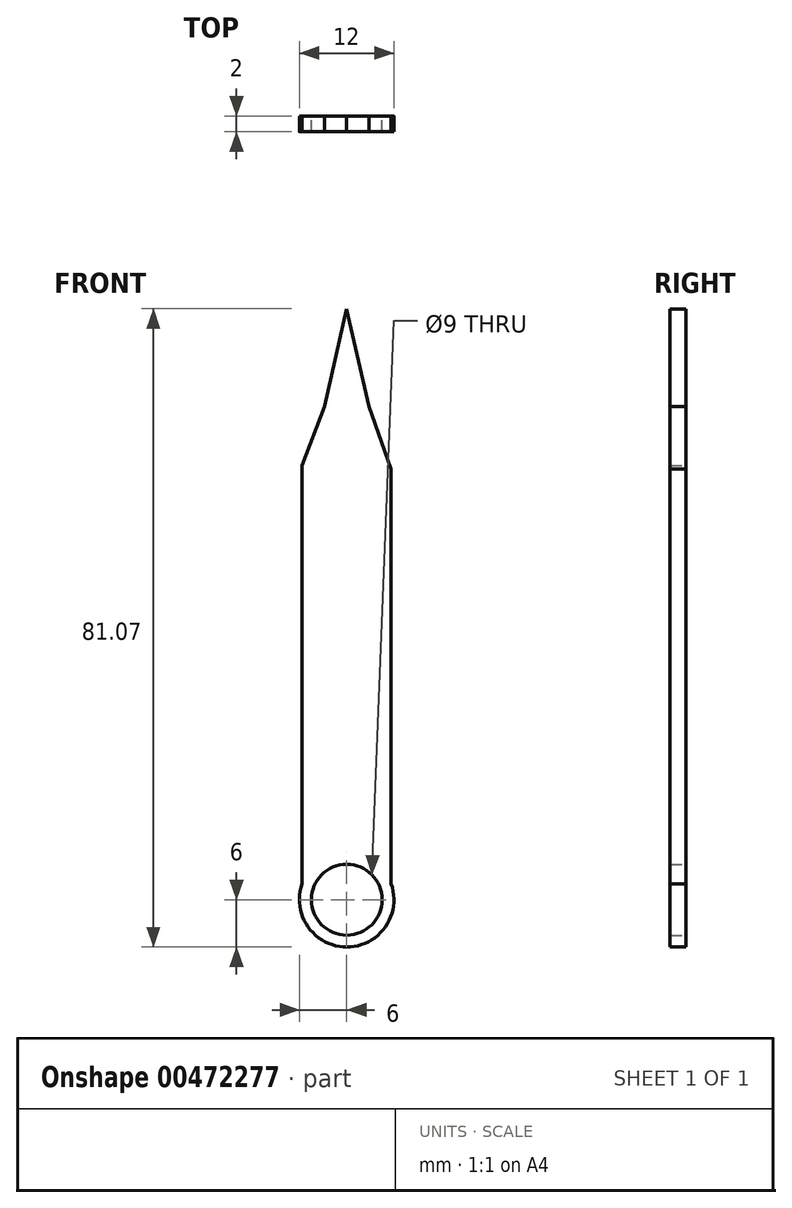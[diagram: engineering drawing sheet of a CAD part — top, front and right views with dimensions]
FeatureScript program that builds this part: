
annotation { "Feature Type Name" : "Feature", "Feature Type Description" : "" }
export const myFeature = defineFeature(function(context is Context, id is Id, definition is map)
    precondition{}
    {
        {
            var Q0;
            Q0=qCreatedBy(makeId("Front.planeOp"),FACE);
            var sketch = newSketch(context, id + "F0", { "sketchPlane" : qUnion([Q0])});
            skArc(sketch, "E0", {"start": v(-5.65, 2.02) * mm, "mid": v(0, -6) * mm, "end": v(5.65, 2.02) * mm});
            skCircle(sketch, "E1", {"center": v(0, 0) * mm, "radius": 4.5 * mm});
            skLineSegment(sketch, "E2", {"start": v(-5.65, 2.02) * mm, "end": v(-5.65, 55.2) * mm});
            skLineSegment(sketch, "E3", {"start": v(5.65, 2.02) * mm, "end": v(5.65, 54.69) * mm});
            skLineSegment(sketch, "E4", {"start": v(-5.65, 55.2) * mm, "end": v(-2.82, 62.66) * mm});
            skLineSegment(sketch, "E5", {"start": v(5.65, 54.69) * mm, "end": v(2.82, 62.66) * mm});
            skPoint(sketch, "E6.orphan", {"position": v(-5.65, 62.66) * mm});
            skPoint(sketch, "E7.orphan", {"position": v(5.65, 62.66) * mm});
            skLineSegment(sketch, "E8", {"start": v(-2.82, 62.66) * mm, "end": v(0, 75.07) * mm});
            skLineSegment(sketch, "E9", {"start": v(0, 75.07) * mm, "end": v(2.82, 62.66) * mm});
            skPoint(sketch, "E10.end.orphan", {"position": v(0, 62.66) * mm});
            skSolve(sketch);
        }
        {
            var Q0;
            Q0 = qSketchRegion(id + "F0", true);
            extrude(context, id + "F1", {"entities" : qUnion([Q0]), "depth" : 2 * mm, "offsetDistance" : 25 * mm});
        }
    });
